# Revit family: HIGHTECH
name_source: partatom
category: Осветительные приборы
units: mm (PartAtom-declared; Revit-internal decimal feet)

## family parameters
Всегда вертикально = Нет
Источник света = Да
На основе рабочей плоскости = Нет
Общий = Нет
При загрузке вырезать с полостями = Нет
Размер круглого соединителя = Использовать диаметр
Тип детали = Нормальный
Точка расчета площади = Да

## types (32) — shared parameters
ADSK_Единица измерения = шт.
ADSK_Завод-изготовитель = ЗАО «Центрстройсвет»
ADSK_Классификация нагрузок = Прочее
ADSK_Количество фаз = 1
ADSK_Количество фаз числовое = 1
ADSK_Коэффициент мощности = 0.92
ADSK_Напряжение = 230 В
ADSK_Ток = 0 А
URL = http://csvt.ru
Видимая форма излучения при визуализации = Да
Высота = 40 мм
Изготовитель = ЗАО «Центрстройсвет»
Материал светильника = RAL 9001
Материал стекла = RAL светящийся
Матриал вставок = RAL 9006
Светофильтр = 16777215
Смещение цветовой температуры при затухании лампы = <Нет>
Угол наклона = 90.00°

## per-type parameters (varying)
| type | ADSK_Код изделия | ADSK_Масса | ADSK_Наименование | ADSK_Номинальная мощность | ADSK_Обозначение | ADSK_Полная мощность | Длина | Излучение по длине прямоугольника | Излучение по ширине прямоугольника | Файл фотометрической сетки | Ширина |
| Hightech-76/opal-sand 160х2300 (IP54, 4000К, белый) | ЦБ000007745 | 2.9 | Универсальный светодиодный светильник Hightech-76/opal-sand 160х2300 (IP54, 4000К, белый) | 76 Вт | Hightech-76/opal-sand 160х2300 (IP54, 4000К, белый) | 83 В·А | 2300 мм | 2260 мм | 120 мм | Светильник HIGHTECH-76 OPAL-SAND-(160x2300).IES | 160 мм |
| Hightech-76/opal-sand 160х2300 (IP40, 4000К, белый) | ЦБ000009678 | 2.9 | Универсальный светодиодный светильник Hightech-76/opal-sand 160х2300 (IP40, 4000К, белый) | 76 Вт | Hightech-76/opal-sand 160х2300 (IP40, 4000К, белый) | 83 В·А | 2300 мм | 2260 мм | 120 мм | Светильник HIGHTECH-76 OPAL-SAND-(160x2300).IES | 160 мм |
| Hightech-38/opal-sand 160х1195 (IP54, 4000К, белый) c БАП на 3 часа | ЦБ000007739 | 1.6 | Универсальный светодиодный светильник Hightech-38/opal-sand 160х1195 (IP54, 4000К, белый) c БАП на 3 часа | 38 Вт | Hightech-38/opal-sand 160х1195 (IP54, 4000К, белый) | 41 В·А | 1195 мм | 1155 мм | 120 мм | Светильник HIGHTECH-38 OPAL-SAND-(160x1195).IES | 160 мм |
| Hightech-38/opal-sand 160х1195 (IP54, 4000К, белый) c БАП на 1 час | ЦБ000007731 | 1.6 | Универсальный светодиодный светильник Hightech-38/opal-sand 160х1195 (IP54, 4000К, белый) c БАП на 1 час | 38 Вт | Hightech-38/opal-sand 160х1195 (IP54, 4000К, белый) | 41 В·А | 1195 мм | 1155 мм | 120 мм | Светильник HIGHTECH-38 OPAL-SAND-(160x1195).IES | 160 мм |
| Hightech-38/opal-sand 160х1195 (IP54, 4000К, белый) | ЦБ000009677 | 1.6 | Универсальный светодиодный светильник Hightech-38/opal-sand 160х1195 (IP54, 4000К, белый) | 38 Вт | Hightech-38/opal-sand 160х1195 (IP54, 4000К, белый) | 41 В·А | 1195 мм | 1155 мм | 120 мм | Светильник HIGHTECH-38 OPAL-SAND-(160x1195).IES | 160 мм |
| Hightech-38/opal-sand 160х1195 (IP40, 4000К, белый) c БАП на 3 часа | ЦБ000007735 | 1.6 | Универсальный светодиодный светильник Hightech-38/opal-sand 160х1195 (IP40, 4000К, белый) c БАП на 3 час | 38 Вт | Hightech-38/opal-sand 160х1195 (IP40, 4000К, белый) | 41 В·А | 1195 мм | 1155 мм | 120 мм | Светильник HIGHTECH-38 OPAL-SAND-(160x1195).IES | 160 мм |
| Hightech-38/opal-sand 160х1195 (IP40, 4000К, белый) c БАП на 1 час | ЦБ000007725 | 1.6 | Универсальный светодиодный светильник Hightech-38/opal-sand 160х1195 (IP40, 4000К, белый) c БАП на 1 час | 38 Вт | Hightech-38/opal-sand 160х1195 (IP40, 4000К, белый) | 41 В·А | 1195 мм | 1155 мм | 120 мм | Светильник HIGHTECH-38 OPAL-SAND-(160x1195).IES | 160 мм |
| Hightech-38/opal-sand 160х1195 (IP40, 4000К, белый) | ЦБ000009675 | 1.6 | Универсальный светодиодный светильник Hightech-38/opal-sand 160х1195 (IP40, 4000К, белый) | 38 Вт | Hightech-38/opal-sand 160х1195 (IP40, 4000К, белый) | 41 В·А | 1195 мм | 1155 мм | 120 мм | Светильник HIGHTECH-38 OPAL-SAND-(160x1195).IES | 160 мм |
| Hightech-76/opal-sand 595х1195 (IP54, 4000К, белый) | ЦБ000007618 | 5 | Универсальный светодиодный светильник Hightech-76/opal-sand 595х1195 (IP54, 4000К, белый) | 76 Вт | Hightech-76/opal-sand 595х1195 (IP54, 4000К, белый) | 83 В·А | 1195 мм | 1155 мм | 555 мм | Светильник HIGHTECH-76 OPAL-SAND-(595x1195).IES | 595 мм |
| Hightech-76/opal-sand 595х1195 (IP40, 4000К, белый) | ЦБ000007380 | 5 | Универсальный светодиодный светильник Hightech-76/opal-sand 595х1195 (IP40, 4000К, белый) | 76 Вт | Hightech-76/opal-sand 595х1195 (IP40, 4000К, белый) | 83 В·А | 1195 мм | 1155 мм | 555 мм | Светильник HIGHTECH-76 OPAL-SAND-(595x1195).IES | 595 мм |
| Hightech-76/opal-sand 295х1195 (IP54, 4000К, белый) | ЦБ000007600 | 2.5 | Универсальный светодиодный светильник Hightech-76/opal-sand 295х1195 (IP54, 4000К, белый) | 76 Вт | Hightech-76/opal-sand 295х1195 (IP54, 4000К, белый) | 83 В·А | 1195 мм | 1155 мм | 255 мм | Светильник HIGHTECH-76 OPAL-SAND-(295x1195).ies | 295 мм |
| Hightech-76/opal-sand 295х1195 (IP40, 4000К, белый) | ЦБ000007594 | 2.5 | Универсальный светодиодный светильник Hightech-76/opal-sand 295х1195 (IP40, 4000К, белый) | 76 Вт | Hightech-76/opal-sand 295х1195 (IP40, 4000К, белый) | 83 В·А | 1195 мм | 1155 мм | 255 мм | Светильник HIGHTECH-76 OPAL-SAND-(295x1195).ies | 295 мм |
| Hightech-50/opal-sand 595x595 (IP54, 4000К, белый) | ЦБ000007383 | 2.5 | Универсальный светодиодный светильник Hightech-50/opal-sand 595x595 (IP54, 4000К, белый) | 50 Вт | Hightech-50/opal-sand 595x595 (IP54, 4000К, белый) | 54 В·А | 595 мм | 555 мм | 555 мм | Светильник HIGHTECH-50 OPAL-SAND-(595x595).IES | 595 мм |
| Hightech-50/opal-sand 595х595 (IP40, 4000К, белый) | ЦБ000007370 | 2.5 | Универсальный светодиодный светильник Hightech-50/opal-sand 595х595 (IP40, 4000К, белый) | 50 Вт | Hightech-50/opal-sand 595х595 (IP40, 4000К, белый) | 54 В·А | 595 мм | 555 мм | 555 мм | Светильник HIGHTECH-50 OPAL-SAND-(595x595).IES | 595 мм |
| Hightech-38/opal-sand 595х595 (IP54, 4000К, белый) c БАП на 3 часа | ЦБ000007551 | 2.5 | Универсальный светодиодный светильник Hightech-38/opal-sand 595х595 (IP54, 4000К, белый) c БАП на 3 часа | 38 Вт | Hightech-38/opal-sand 595х595 (IP54, 4000К, белый) | 41 В·А | 595 мм | 555 мм | 555 мм | Светильник HIGHTECH-38 OPAL-SAND-(595x595).IES | 595 мм |
| Hightech-38/opal-sand 595х595 (IP54, 4000К, белый) c БАП на 1 час | ЦБ000007543 | 2.5 | Универсальный светодиодный светильник Hightech-38/opal-sand 595х595 (IP54, 4000К, белый) c БАП на 1 час | 38 Вт | Hightech-38/opal-sand 595х595 (IP54, 4000К, белый) | 41 В·А | 595 мм | 555 мм | 555 мм | Светильник HIGHTECH-38 OPAL-SAND-(595x595).IES | 595 мм |
| Hightech-38/opal-sand 595х595 (IP54, 4000К, белый) | ЦБ000007381 | 2.5 | Универсальный светодиодный светильник Hightech-38/opal-sand 595х595 (IP54, 4000К, белый) | 38 Вт | Hightech-38/opal-sand 595х595 (IP54, 4000К, белый) | 41 В·А | 595 мм | 555 мм | 555 мм | Светильник HIGHTECH-38 OPAL-SAND-(595x595).IES | 595 мм |
| Hightech-38/opal-sand 595х595 (IP40, 4000К, белый) c БАП на 3 часа | ЦБ000007547 | 2.5 | Универсальный светодиодный светильник Hightech-38/opal-sand 595х595 (IP40, 4000К, белый) c БАП на 3 час | 38 Вт | Hightech-38/opal-sand 595х595 (IP40, 4000К, белый) | 41 В·А | 595 мм | 555 мм | 555 мм | Светильник HIGHTECH-38 OPAL-SAND-(595x595).IES | 595 мм |
| Hightech-38/opal-sand 595х595 (IP40, 4000К, белый) c БАП на 1 час | ЦБ000007540 | 2.5 | Универсальный светодиодный светильник Hightech-38/opal-sand 595х595 (IP40, 4000К, белый) c БАП на 1 час | 38 Вт | Hightech-38/opal-sand 595х595 (IP40, 4000К, белый) | 41 В·А | 595 мм | 555 мм | 555 мм | Светильник HIGHTECH-38 OPAL-SAND-(595x595).IES | 595 мм |
| Hightech-38/opal-sand 595х595 (IP40, 4000К, белый) | ЦБ000007368 | 2.5 | Универсальный светодиодный светильник Hightech-38/opal-sand 595х595 (IP40, 4000К, белый) | 38 Вт | Hightech-38/opal-sand 595х595 (IP40, 4000К, белый) | 41 В·А | 595 мм | 555 мм | 555 мм | Светильник HIGHTECH-38 OPAL-SAND-(595x595).IES | 595 мм |
| Hightech-38/opal-sand 295х1195 (IP54, 4000К, белый) c БАП на 3 часа | ЦБ000008596 | 2.5 | Универсальный светодиодный светильник Hightech-38/opal-sand 295х1195 (IP54, 4000К, белый) c БАП на 3 час | 38 Вт | Hightech-38/opal-sand 295х1195 (IP54, 4000К, белый) | 41 В·А | 1195 мм | 1155 мм | 255 мм | Светильник HIGHTECH-38 OPAL-SAND-(295x1195).ies | 295 мм |
| Hightech-38/opal-sand 295х1195 (IP54, 4000К, белый) c БАП на 1 час | ЦБ000007612 | 2.5 | Универсальный светодиодный светильник Hightech-38/opal-sand 295х1195 (IP54, 4000К, белый) c БАП на 1 час | 38 Вт | Hightech-38/opal-sand 295х1195 (IP54, 4000К, белый) | 41 В·А | 1195 мм | 1155 мм | 255 мм | Светильник HIGHTECH-38 OPAL-SAND-(295x1195).ies | 295 мм |
| Hightech-38/opal-sand 295х1195 (IP54, 4000К, белый) | ЦБ000007604 | 2.5 | Универсальный светодиодный светильник Hightech-38/opal-sand 295х1195 (IP54, 4000К, белый) | 38 Вт | Hightech-38/opal-sand 295х1195 (IP54, 4000К, белый) | 41 В·А | 1195 мм | 1155 мм | 255 мм | Светильник HIGHTECH-38 OPAL-SAND-(295x1195).ies | 295 мм |
| Hightech-38/opal-sand 295х1195 (IP40, 4000К, белый) c БАП на 3 часа | ЦБ000008592 | 2.5 | Универсальный светодиодный светильник Hightech-38/opal-sand 295х1195 (IP40, 4000К, белый) c БАП на 3 час | 38 Вт | Hightech-38/opal-sand 295х1195 (IP40, 4000К, белый) | 41 В·А | 1195 мм | 1155 мм | 255 мм | Светильник HIGHTECH-38 OPAL-SAND-(295x1195).ies | 295 мм |
| Hightech-38/opal-sand 295х1195 (IP40, 4000К, белый) c БАП на 1 час | ЦБ000007608 | 2.5 | Универсальный светодиодный светильник Hightech-38/opal-sand 295х1195 (IP40, 4000К, белый) c БАП на 1 час | 38 Вт | Hightech-38/opal-sand 295х1195 (IP40, 4000К, белый) | 41 В·А | 1195 мм | 1155 мм | 255 мм | Светильник HIGHTECH-38 OPAL-SAND-(295x1195).ies | 295 мм |
| Hightech-30/opal-sand 295х595 (IP54, 4000К, белый) c БАП на 3 часа | ЦБ000007585 | 1.4 | Универсальный светодиодный светильник Hightech-30/opal-sand 295х595 (IP54, 4000К, белый) c БАП на 3 час | 30 Вт | Hightech-30/opal-sand 295х595 (IP54, 4000К, белый) | 33 В·А | 595 мм | 555 мм | 255 мм | Светильник HIGHTECH-30 OPAL-SAND-(295x595).IES | 295 мм |
| Hightech-30/opal-sand 295х595 (IP54, 4000К, белый) c БАП на 1 час | ЦБ000007577 | 1.4 | Универсальный светодиодный светильник Hightech-30/opal-sand 295х595 (IP54, 4000К, белый) c БАП на 1 час | 30 Вт | Hightech-30/opal-sand 295х595 (IP54, 4000К, белый) | 33 В·А | 595 мм | 555 мм | 255 мм | Светильник HIGHTECH-30 OPAL-SAND-(295x595).IES | 295 мм |
| Hightech-30/opal-sand 295х595 (IP54, 4000К, белый) | ЦБ000007569 | 1.4 | Универсальный светодиодный светильник Hightech-30/opal-sand 295х595 (IP54, 4000К, белый) | 30 Вт | Hightech-30/opal-sand 295х595 (IP54, 4000К, белый) | 33 В·А | 595 мм | 555 мм | 255 мм | Светильник HIGHTECH-30 OPAL-SAND-(295x595).IES | 295 мм |
| Hightech-30/opal-sand 295х595 (IP40, 4000К, белый) c БАП на 3 часа | ЦБ000007581 | 1.4 | Универсальный светодиодный светильник Hightech-30/opal-sand 295х595 (IP40, 4000К, белый) c БАП на 3 час | 30 Вт | Hightech-30/opal-sand 295х595 (IP40, 4000К, белый) | 33 В·А | 595 мм | 555 мм | 255 мм | Светильник HIGHTECH-30 OPAL-SAND-(295x595).IES | 295 мм |
| Hightech-30/opal-sand 295х595 (IP40, 4000К, белый) c БАП на 1 час | ЦБ000007573 | 1.4 | Универсальный светодиодный светильник Hightech-30/opal-sand 295х595 (IP40, 4000К, белый) c БАП на 1 час. | 30 Вт | Hightech-30/opal-sand 295х595 (IP40, 4000К, белый) | 33 В·А | 595 мм | 555 мм | 255 мм | Светильник HIGHTECH-30 OPAL-SAND-(295x595).IES | 295 мм |
| Hightech-38/opal-sand 295х1195 (IP40, 4000К, белый) | ЦБ000007589 | 2.5 | Универсальный светодиодный светильник Hightech-38/opal-sand 295х1195 (IP40, 4000К, белый) | 38 Вт | Hightech-38/opal-sand 295х1195 (IP40, 4000К, белый) | 41 В·А | 1195 мм | 1155 мм | 255 мм | Светильник HIGHTECH-38 OPAL-SAND-(295x1195).ies | 295 мм |
| Hightech-30/opal-sand 295х595 (IP40, 4000К, белый) | ЦБ000007366 | 1.4 | Универсальный светодиодный светильник Hightech-30/opal-sand 295х595 (IP40, 4000К, белый) | 30 Вт | Hightech-30/opal-sand 295х595 (IP40, 4000К, белый) | 33 В·А | 595 мм | 555 мм | 255 мм | Светильник HIGHTECH-30 OPAL-SAND-(295x595).IES | 295 мм |
